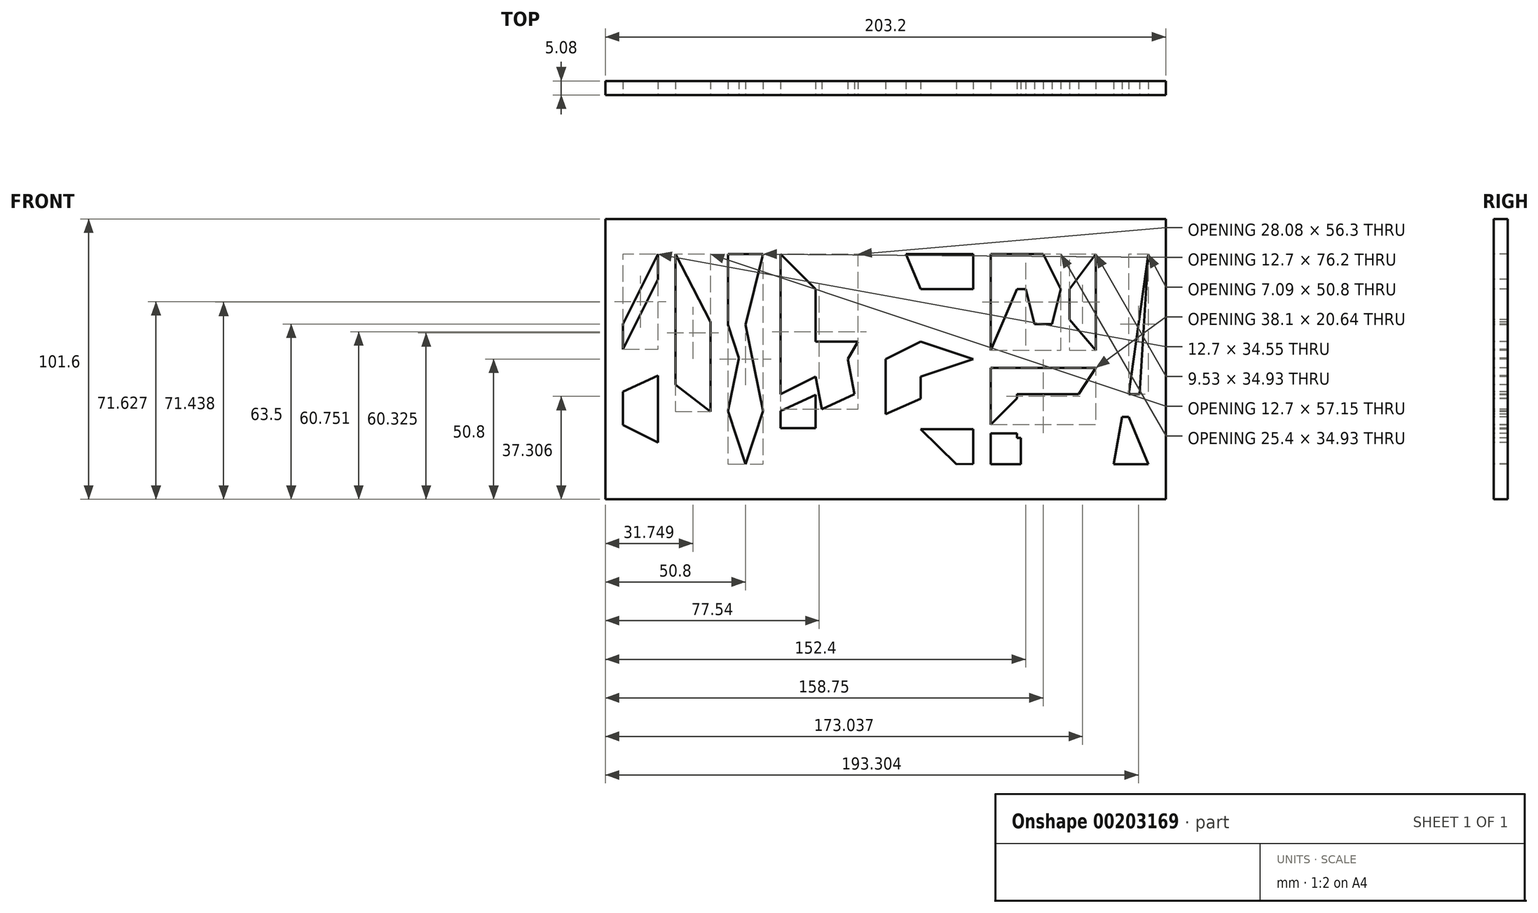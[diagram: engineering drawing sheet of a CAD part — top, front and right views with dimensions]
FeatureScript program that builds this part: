
annotation { "Feature Type Name" : "Feature", "Feature Type Description" : "" }
export const myFeature = defineFeature(function(context is Context, id is Id, definition is map)
    precondition{}
    {
        {
            var Q0;
            Q0=qCreatedBy(makeId("Front.planeOp"),FACE);
            var sketch = newSketch(context, id + "F0", { "sketchPlane" : qUnion([Q0])});
            skLineSegment(sketch, "E0.bottom", {"start": v(0, 0) * mm, "end": v(220.66, 0) * mm, "construction": true});
            skLineSegment(sketch, "E0.top", {"start": v(0, 138.11) * mm, "end": v(220.66, 138.11) * mm, "construction": true});
            skLineSegment(sketch, "E0.left", {"start": v(0, 0) * mm, "end": v(0, 138.11) * mm, "construction": true});
            skLineSegment(sketch, "E0.right", {"start": v(220.66, 0) * mm, "end": v(220.66, 138.11) * mm, "construction": true});
            skSolve(sketch);
        }
        {
            var Q0;
            Q0=qCreatedBy(makeId("Front.planeOp"),FACE);
            var sketch = newSketch(context, id + "F1", { "sketchPlane" : qUnion([Q0])});
            skLineSegment(sketch, "E1.bottom", {"start": v(0, 0) * mm, "end": v(203.2, 0) * mm});
            skLineSegment(sketch, "E1.top", {"start": v(0, 101.6) * mm, "end": v(203.2, 101.6) * mm});
            skLineSegment(sketch, "E1.left", {"start": v(0, 0) * mm, "end": v(0, 101.6) * mm});
            skLineSegment(sketch, "E1.right", {"start": v(203.2, 0) * mm, "end": v(203.2, 101.6) * mm});
            skSolve(sketch);
        }
        {
            var Q0;
            Q0=makeQuery(id+"F1.imprint","IMPRINT",FACE,{"disambiguationData":[TD([[makeQuery(id+"F1.imprint","IMPRINT",EDGE,{"derivedFrom":sQuery(id+"F1.wireOp",EDGE,"E1.bottom")}),1.0]])]});
            extrude(context, id + "F2", {"entities" : qUnion([Q0]), "oppositeDirection" : true, "depth" : 5.08 * mm});
        }
        {
            var Q0;
            Q0=makeQuery(id+"F2.opExtrude","CAP_FACE",FACE,{"disambiguationData":[OSD([sQuery(id+"F1.wireOp",EDGE,"E1.bottom"),sQuery(id+"F1.wireOp",EDGE,"E1.top"),sQuery(id+"F1.wireOp",EDGE,"E1.left"),sQuery(id+"F1.wireOp",EDGE,"E1.right")])],"isStart":true});
            var sketch = newSketch(context, id + "F3", { "sketchPlane" : qUnion([Q0])});
            skLineSegment(sketch, "E2", {"start": v(0, 50.8) * mm, "end": v(203.2, 50.8) * mm, "construction": true});
            skLineSegment(sketch, "E3", {"start": v(6.35, 88.9) * mm, "end": v(19.05, 88.9) * mm});
            skLineSegment(sketch, "E4", {"start": v(19.05, 88.9) * mm, "end": v(19.05, 50.8) * mm});
            skLineSegment(sketch, "E5", {"start": v(19.05, 50.8) * mm, "end": v(25.4, 50.8) * mm});
            skLineSegment(sketch, "E6", {"start": v(25.4, 50.8) * mm, "end": v(25.4, 88.9) * mm});
            skLineSegment(sketch, "E7", {"start": v(25.4, 88.9) * mm, "end": v(38.1, 88.9) * mm});
            skLineSegment(sketch, "E8", {"start": v(38.1, 88.9) * mm, "end": v(38.1, 50.8) * mm});
            skLineSegment(sketch, "E9", {"start": v(38.1, 50.8) * mm, "end": v(38.1, 12.7) * mm});
            skLineSegment(sketch, "E10", {"start": v(38.1, 12.7) * mm, "end": v(25.4, 12.7) * mm});
            skLineSegment(sketch, "E11", {"start": v(25.4, 12.7) * mm, "end": v(25.4, 31.75) * mm});
            skLineSegment(sketch, "E12", {"start": v(25.4, 31.75) * mm, "end": v(19.05, 31.75) * mm});
            skLineSegment(sketch, "E13", {"start": v(19.05, 31.75) * mm, "end": v(19.05, 12.7) * mm});
            skLineSegment(sketch, "E14", {"start": v(19.05, 12.7) * mm, "end": v(6.35, 12.7) * mm});
            skLineSegment(sketch, "E15", {"start": v(44.45, 88.9) * mm, "end": v(44.45, 12.7) * mm});
            skLineSegment(sketch, "E16", {"start": v(44.45, 12.7) * mm, "end": v(57.15, 12.7) * mm});
            skLineSegment(sketch, "E17", {"start": v(57.15, 12.7) * mm, "end": v(57.15, 88.9) * mm});
            skLineSegment(sketch, "E18", {"start": v(57.15, 88.9) * mm, "end": v(44.45, 88.9) * mm});
            skLineSegment(sketch, "E19", {"start": v(63.5, 88.9) * mm, "end": v(63.5, 12.7) * mm});
            skPoint(sketch, "E19.startSnap0", {"position": v(50.8, 88.9) * mm});
            skLineSegment(sketch, "E20", {"start": v(63.5, 12.7) * mm, "end": v(76.2, 12.7) * mm});
            skLineSegment(sketch, "E21", {"start": v(76.2, 12.7) * mm, "end": v(76.2, 44.45) * mm});
            skLineSegment(sketch, "E22", {"start": v(76.2, 44.45) * mm, "end": v(82.32, 12.7) * mm});
            skLineSegment(sketch, "E23", {"start": v(82.32, 12.7) * mm, "end": v(95.25, 12.7) * mm});
            skLineSegment(sketch, "E24", {"start": v(95.25, 12.7) * mm, "end": v(87.91, 50.8) * mm});
            skLineSegment(sketch, "E25", {"start": v(87.91, 50.8) * mm, "end": v(95.25, 63.5) * mm});
            skLineSegment(sketch, "E26", {"start": v(95.25, 63.5) * mm, "end": v(95.25, 88.9) * mm});
            skLineSegment(sketch, "E27", {"start": v(95.25, 88.9) * mm, "end": v(63.5, 88.9) * mm});
            skLineSegment(sketch, "E28", {"start": v(101.6, 88.9) * mm, "end": v(101.6, 12.7) * mm});
            skLineSegment(sketch, "E29", {"start": v(101.6, 12.7) * mm, "end": v(133.35, 12.7) * mm});
            skLineSegment(sketch, "E30", {"start": v(133.35, 12.7) * mm, "end": v(133.35, 25.4) * mm});
            skLineSegment(sketch, "E31", {"start": v(133.35, 25.4) * mm, "end": v(114.3, 25.4) * mm});
            skLineSegment(sketch, "E32", {"start": v(114.3, 25.4) * mm, "end": v(114.3, 44.45) * mm});
            skLineSegment(sketch, "E33", {"start": v(114.3, 44.45) * mm, "end": v(133.35, 44.45) * mm});
            skLineSegment(sketch, "E34", {"start": v(133.35, 44.45) * mm, "end": v(133.35, 57.15) * mm});
            skLineSegment(sketch, "E35", {"start": v(133.35, 57.15) * mm, "end": v(114.3, 57.15) * mm});
            skLineSegment(sketch, "E36", {"start": v(114.3, 57.15) * mm, "end": v(114.3, 76.2) * mm});
            skLineSegment(sketch, "E37", {"start": v(114.3, 76.2) * mm, "end": v(133.35, 76.2) * mm});
            skLineSegment(sketch, "E38", {"start": v(133.35, 76.2) * mm, "end": v(133.35, 88.9) * mm});
            skLineSegment(sketch, "E39", {"start": v(133.35, 88.9) * mm, "end": v(101.6, 88.9) * mm});
            skLineSegment(sketch, "E40", {"start": v(139.7, 88.9) * mm, "end": v(177.8, 88.9) * mm});
            skLineSegment(sketch, "E41", {"start": v(177.8, 88.9) * mm, "end": v(177.8, 53.98) * mm});
            skLineSegment(sketch, "E42", {"start": v(168.28, 53.98) * mm, "end": v(168.28, 76.2) * mm});
            skLineSegment(sketch, "E43", {"start": v(149.23, 76.2) * mm, "end": v(149.23, 53.98) * mm});
            skLineSegment(sketch, "E44", {"start": v(139.7, 12.7) * mm, "end": v(177.8, 12.7) * mm});
            skLineSegment(sketch, "E45", {"start": v(177.8, 12.7) * mm, "end": v(177.8, 22.23) * mm});
            skLineSegment(sketch, "E46", {"start": v(177.8, 22.23) * mm, "end": v(149.23, 22.23) * mm});
            skLineSegment(sketch, "E47", {"start": v(149.23, 22.23) * mm, "end": v(149.23, 23.81) * mm});
            skLineSegment(sketch, "E48", {"start": v(149.23, 36.51) * mm, "end": v(149.23, 38.1) * mm});
            skLineSegment(sketch, "E49", {"start": v(149.23, 38.1) * mm, "end": v(177.8, 38.1) * mm});
            skLineSegment(sketch, "E50", {"start": v(177.8, 38.1) * mm, "end": v(177.8, 47.63) * mm});
            skLineSegment(sketch, "E51", {"start": v(6.35, 88.9) * mm, "end": v(6.35, 12.7) * mm});
            skLineSegment(sketch, "E52", {"start": v(149.23, 76.2) * mm, "end": v(152.4, 76.2) * mm});
            skLineSegment(sketch, "E53", {"start": v(152.4, 76.2) * mm, "end": v(155.57, 63.5) * mm});
            skLineSegment(sketch, "E54", {"start": v(155.57, 63.5) * mm, "end": v(161.93, 63.5) * mm});
            skLineSegment(sketch, "E55", {"start": v(161.93, 63.5) * mm, "end": v(165.1, 76.2) * mm});
            skLineSegment(sketch, "E56", {"start": v(165.1, 76.2) * mm, "end": v(168.28, 76.2) * mm});
            skPoint(sketch, "E57", {"position": v(158.75, 88.9) * mm});
            skPoint(sketch, "E58", {"position": v(158.75, 63.5) * mm});
            skLineSegment(sketch, "E59", {"start": v(161.93, 33.34) * mm, "end": v(161.93, 26.99) * mm});
            skPoint(sketch, "E60", {"position": v(161.93, 30.16) * mm});
            skLineSegment(sketch, "E61", {"start": v(139.7, 88.9) * mm, "end": v(139.7, 53.98) * mm});
            skLineSegment(sketch, "E62", {"start": v(139.7, 53.98) * mm, "end": v(149.23, 53.98) * mm});
            skLineSegment(sketch, "E63", {"start": v(168.28, 53.98) * mm, "end": v(177.8, 53.98) * mm});
            skLineSegment(sketch, "E64", {"start": v(139.7, 47.63) * mm, "end": v(177.8, 47.63) * mm});
            skLineSegment(sketch, "E65", {"start": v(139.7, 47.63) * mm, "end": v(139.7, 12.7) * mm});
            skLineSegment(sketch, "E66", {"start": v(161.93, 33.34) * mm, "end": v(149.23, 36.51) * mm});
            skLineSegment(sketch, "E67", {"start": v(149.23, 23.81) * mm, "end": v(161.93, 26.99) * mm});
            skPoint(sketch, "E68", {"position": v(139.7, 30.16) * mm});
            skLineSegment(sketch, "E69", {"start": v(184.15, 88.9) * mm, "end": v(196.85, 88.9) * mm});
            skLineSegment(sketch, "E70", {"start": v(196.85, 88.9) * mm, "end": v(193.67, 38.1) * mm});
            skLineSegment(sketch, "E71", {"start": v(193.67, 38.1) * mm, "end": v(187.33, 38.1) * mm});
            skLineSegment(sketch, "E72", {"start": v(187.33, 38.1) * mm, "end": v(184.15, 88.9) * mm});
            skPoint(sketch, "E73", {"position": v(190.5, 88.9) * mm});
            skPoint(sketch, "E74", {"position": v(190.5, 38.1) * mm});
            skLineSegment(sketch, "E75", {"start": v(187.32, 29.85) * mm, "end": v(184.15, 12.7) * mm});
            skLineSegment(sketch, "E76", {"start": v(184.15, 12.7) * mm, "end": v(196.85, 12.7) * mm});
            skLineSegment(sketch, "E77", {"start": v(196.85, 12.7) * mm, "end": v(193.68, 29.85) * mm});
            skLineSegment(sketch, "E78", {"start": v(193.67, 29.85) * mm, "end": v(187.33, 29.85) * mm});
            skPoint(sketch, "E79", {"position": v(190.5, 29.85) * mm});
            skPoint(sketch, "E80", {"position": v(190.5, 12.7) * mm});
            skLineSegment(sketch, "E81", {"start": v(76.2, 57.15) * mm, "end": v(76.2, 76.2) * mm});
            skLineSegment(sketch, "E82", {"start": v(76.2, 76.2) * mm, "end": v(83.54, 76.2) * mm});
            skLineSegment(sketch, "E83", {"start": v(83.54, 76.2) * mm, "end": v(83.54, 69.85) * mm});
            skLineSegment(sketch, "E84", {"start": v(83.54, 69.85) * mm, "end": v(76.2, 57.15) * mm});
            skSolve(sketch);
        }
        {
            var Q0;
            Q0=makeQuery(id+"F3.imprint","IMPRINT",FACE,{"disambiguationData":[TD([[makeQuery(id+"F3.imprint","IMPRINT",EDGE,{"derivedFrom":sQuery(id+"F3.wireOp",EDGE,"E3")}),1.0]])]});
            var sketch = newSketch(context, id + "F4", { "sketchPlane" : qUnion([Q0])});
            skLineSegment(sketch, "E85", {"start": v(6.35, 63.49) * mm, "end": v(19.05, 88.9) * mm});
            skLineSegment(sketch, "E86", {"start": v(19.05, 88.9) * mm, "end": v(6.35, 88.9) * mm});
            skLineSegment(sketch, "E87", {"start": v(6.35, 88.9) * mm, "end": v(6.35, 63.49) * mm});
            skLineSegment(sketch, "E88", {"start": v(6.35, 54.35) * mm, "end": v(19.05, 79.76) * mm});
            skLineSegment(sketch, "E89", {"start": v(19.05, 79.76) * mm, "end": v(19.05, 50.8) * mm});
            skLineSegment(sketch, "E90", {"start": v(6.35, 38.97) * mm, "end": v(6.35, 54.35) * mm});
            skLineSegment(sketch, "E91", {"start": v(19.05, 31.75) * mm, "end": v(19.05, 44.79) * mm});
            skLineSegment(sketch, "E92", {"start": v(25.4, 41.55) * mm, "end": v(38.1, 31.75) * mm});
            skLineSegment(sketch, "E93", {"start": v(6.35, 26.94) * mm, "end": v(19.05, 20.6) * mm});
            skLineSegment(sketch, "E94", {"start": v(19.05, 20.6) * mm, "end": v(19.05, 12.7) * mm});
            skLineSegment(sketch, "E95", {"start": v(19.05, 12.7) * mm, "end": v(6.35, 12.7) * mm});
            skLineSegment(sketch, "E96", {"start": v(6.35, 12.7) * mm, "end": v(6.35, 26.94) * mm});
            skLineSegment(sketch, "E97", {"start": v(19.05, 50.8) * mm, "end": v(25.4, 50.8) * mm});
            skLineSegment(sketch, "E98", {"start": v(25.4, 50.8) * mm, "end": v(25.4, 41.55) * mm});
            skLineSegment(sketch, "E99", {"start": v(6.35, 38.97) * mm, "end": v(19.05, 44.79) * mm});
            skLineSegment(sketch, "E100", {"start": v(38.1, 31.75) * mm, "end": v(38.1, 12.7) * mm});
            skLineSegment(sketch, "E101", {"start": v(38.1, 12.7) * mm, "end": v(25.4, 12.7) * mm});
            skLineSegment(sketch, "E102", {"start": v(25.4, 12.7) * mm, "end": v(25.4, 31.75) * mm});
            skLineSegment(sketch, "E103", {"start": v(25.4, 31.75) * mm, "end": v(19.05, 31.75) * mm});
            skLineSegment(sketch, "E104", {"start": v(25.4, 64.16) * mm, "end": v(25.4, 88.9) * mm});
            skLineSegment(sketch, "E105", {"start": v(25.4, 88.9) * mm, "end": v(38.12, 64.16) * mm});
            skLineSegment(sketch, "E106", {"start": v(38.12, 64.16) * mm, "end": v(25.4, 64.16) * mm});
            skLineSegment(sketch, "E107", {"start": v(44.45, 88.9) * mm, "end": v(44.45, 63.26) * mm});
            skLineSegment(sketch, "E108", {"start": v(44.45, 63.26) * mm, "end": v(48.35, 51.2) * mm});
            skLineSegment(sketch, "E109", {"start": v(48.35, 51.2) * mm, "end": v(44.45, 31.96) * mm});
            skLineSegment(sketch, "E110", {"start": v(44.45, 31.96) * mm, "end": v(50.8, 12.7) * mm});
            skLineSegment(sketch, "E111", {"start": v(50.8, 12.7) * mm, "end": v(57.15, 31.96) * mm});
            skLineSegment(sketch, "E112", {"start": v(57.15, 31.96) * mm, "end": v(53.25, 51.2) * mm});
            skLineSegment(sketch, "E113", {"start": v(53.25, 51.2) * mm, "end": v(50.8, 63.26) * mm});
            skLineSegment(sketch, "E114", {"start": v(50.8, 63.26) * mm, "end": v(57.15, 88.9) * mm});
            skLineSegment(sketch, "E115", {"start": v(57.15, 88.9) * mm, "end": v(44.45, 88.9) * mm});
            skLineSegment(sketch, "E116", {"start": v(63.5, 88.9) * mm, "end": v(76.2, 76.2) * mm});
            skLineSegment(sketch, "E117", {"start": v(76.2, 76.2) * mm, "end": v(76.2, 57.15) * mm});
            skLineSegment(sketch, "E118", {"start": v(63.5, 38.08) * mm, "end": v(63.5, 88.9) * mm});
            skLineSegment(sketch, "E119", {"start": v(63.5, 25.77) * mm, "end": v(63.5, 31.96) * mm});
            skLineSegment(sketch, "E120", {"start": v(63.5, 31.96) * mm, "end": v(76.2, 37.86) * mm});
            skLineSegment(sketch, "E121", {"start": v(76.2, 37.86) * mm, "end": v(76.2, 25.77) * mm});
            skLineSegment(sketch, "E122", {"start": v(76.2, 25.77) * mm, "end": v(63.5, 25.77) * mm});
            skLineSegment(sketch, "E123", {"start": v(76.2, 57.15) * mm, "end": v(91.58, 57.15) * mm});
            skLineSegment(sketch, "E124", {"start": v(91.58, 57.15) * mm, "end": v(87.91, 50.8) * mm});
            skLineSegment(sketch, "E125", {"start": v(76.2, 44.45) * mm, "end": v(63.5, 38.08) * mm});
            skLineSegment(sketch, "E126", {"start": v(78.48, 32.6) * mm, "end": v(90.35, 38.12) * mm});
            skLineSegment(sketch, "E127", {"start": v(114.3, 57.15) * mm, "end": v(101.6, 50.8) * mm});
            skLineSegment(sketch, "E128", {"start": v(101.6, 50.8) * mm, "end": v(114.3, 44.45) * mm});
            skLineSegment(sketch, "E129", {"start": v(114.3, 44.45) * mm, "end": v(133.35, 50.8) * mm});
            skLineSegment(sketch, "E130", {"start": v(133.35, 50.8) * mm, "end": v(114.3, 57.15) * mm});
            skLineSegment(sketch, "E131", {"start": v(114.3, 36.42) * mm, "end": v(101.6, 30.85) * mm});
            skLineSegment(sketch, "E132", {"start": v(101.6, 30.85) * mm, "end": v(101.6, 12.7) * mm});
            skLineSegment(sketch, "E133", {"start": v(101.6, 12.7) * mm, "end": v(127.23, 12.7) * mm});
            skLineSegment(sketch, "E134", {"start": v(127.23, 12.7) * mm, "end": v(114.3, 25.4) * mm});
            skLineSegment(sketch, "E135", {"start": v(114.3, 25.4) * mm, "end": v(114.3, 36.42) * mm});
            skLineSegment(sketch, "E136", {"start": v(108.95, 88.9) * mm, "end": v(114.3, 76.2) * mm});
            skLineSegment(sketch, "E137", {"start": v(114.3, 76.2) * mm, "end": v(133.35, 76.2) * mm});
            skLineSegment(sketch, "E138", {"start": v(133.35, 76.2) * mm, "end": v(133.35, 88.9) * mm});
            skLineSegment(sketch, "E139", {"start": v(133.35, 88.9) * mm, "end": v(108.95, 88.9) * mm});
            skLineSegment(sketch, "E140", {"start": v(152.4, 76.2) * mm, "end": v(158.75, 88.9) * mm});
            skLineSegment(sketch, "E141", {"start": v(158.75, 88.9) * mm, "end": v(165.1, 76.2) * mm});
            skLineSegment(sketch, "E142", {"start": v(165.1, 76.2) * mm, "end": v(161.93, 63.5) * mm});
            skLineSegment(sketch, "E143", {"start": v(161.93, 63.5) * mm, "end": v(155.57, 63.5) * mm});
            skLineSegment(sketch, "E144", {"start": v(155.57, 63.5) * mm, "end": v(152.4, 76.2) * mm});
            skLineSegment(sketch, "E145", {"start": v(168.28, 76.2) * mm, "end": v(177.8, 88.9) * mm});
            skLineSegment(sketch, "E146", {"start": v(177.8, 88.9) * mm, "end": v(177.8, 53.98) * mm});
            skLineSegment(sketch, "E147", {"start": v(177.8, 53.97) * mm, "end": v(168.27, 65.09) * mm});
            skLineSegment(sketch, "E148", {"start": v(168.28, 65.09) * mm, "end": v(168.28, 76.2) * mm});
            skLineSegment(sketch, "E149", {"start": v(139.7, 53.98) * mm, "end": v(149.23, 53.98) * mm});
            skLineSegment(sketch, "E150", {"start": v(149.23, 53.98) * mm, "end": v(149.23, 76.2) * mm});
            skLineSegment(sketch, "E151", {"start": v(149.23, 76.2) * mm, "end": v(139.7, 53.98) * mm});
            skLineSegment(sketch, "E152", {"start": v(139.7, 47.63) * mm, "end": v(177.8, 47.63) * mm});
            skLineSegment(sketch, "E153", {"start": v(177.8, 47.63) * mm, "end": v(171.66, 38.1) * mm});
            skLineSegment(sketch, "E154", {"start": v(171.66, 38.1) * mm, "end": v(149.23, 38.1) * mm});
            skLineSegment(sketch, "E155", {"start": v(139.7, 47.63) * mm, "end": v(139.7, 26.99) * mm});
            skLineSegment(sketch, "E156", {"start": v(139.7, 26.99) * mm, "end": v(149.23, 36.51) * mm});
            skLineSegment(sketch, "E157", {"start": v(149.23, 36.51) * mm, "end": v(149.23, 38.1) * mm});
            skLineSegment(sketch, "E158", {"start": v(150.7, 22.23) * mm, "end": v(150.7, 12.7) * mm});
            skLineSegment(sketch, "E159", {"start": v(150.7, 12.7) * mm, "end": v(139.7, 12.7) * mm});
            skLineSegment(sketch, "E160", {"start": v(139.7, 12.7) * mm, "end": v(139.7, 23.81) * mm});
            skLineSegment(sketch, "E161", {"start": v(139.7, 23.81) * mm, "end": v(149.23, 23.81) * mm});
            skLineSegment(sketch, "E162", {"start": v(149.23, 23.81) * mm, "end": v(149.23, 22.23) * mm});
            skLineSegment(sketch, "E163", {"start": v(149.23, 22.23) * mm, "end": v(150.7, 22.23) * mm});
            skLineSegment(sketch, "E164", {"start": v(187.33, 38.1) * mm, "end": v(187.33, 88.9) * mm});
            skLineSegment(sketch, "E165", {"start": v(187.33, 88.9) * mm, "end": v(184.15, 88.9) * mm});
            skLineSegment(sketch, "E166", {"start": v(184.15, 88.9) * mm, "end": v(187.33, 38.1) * mm});
            skLineSegment(sketch, "E167", {"start": v(189.76, 29.85) * mm, "end": v(196.85, 12.7) * mm});
            skLineSegment(sketch, "E168", {"start": v(196.85, 12.7) * mm, "end": v(193.68, 29.85) * mm});
            skLineSegment(sketch, "E169", {"start": v(193.68, 29.85) * mm, "end": v(189.76, 29.85) * mm});
            skLineSegment(sketch, "E170", {"start": v(189.76, 38.1) * mm, "end": v(196.85, 88.9) * mm});
            skLineSegment(sketch, "E171", {"start": v(196.85, 88.9) * mm, "end": v(193.68, 38.1) * mm});
            skLineSegment(sketch, "E172", {"start": v(193.67, 38.1) * mm, "end": v(189.76, 38.1) * mm});
            skLineSegment(sketch, "E173", {"start": v(48.35, 51.2) * mm, "end": v(53.25, 51.2) * mm, "construction": true});
            skPoint(sketch, "E174", {"position": v(50.8, 51.2) * mm});
            skLineSegment(sketch, "E175", {"start": v(57.15, 88.9) * mm, "end": v(57.15, 31.96) * mm});
            skLineSegment(sketch, "E176", {"start": v(50.8, 12.7) * mm, "end": v(57.15, 12.7) * mm});
            skLineSegment(sketch, "E177", {"start": v(57.15, 12.7) * mm, "end": v(57.15, 31.96) * mm});
            skLineSegment(sketch, "E178", {"start": v(50.8, 12.7) * mm, "end": v(44.45, 12.7) * mm});
            skLineSegment(sketch, "E179", {"start": v(44.45, 12.7) * mm, "end": v(44.45, 31.96) * mm});
            skLineSegment(sketch, "E180", {"start": v(44.45, 63.26) * mm, "end": v(44.45, 31.96) * mm});
            skLineSegment(sketch, "E181", {"start": v(63.5, 88.9) * mm, "end": v(95.29, 88.9) * mm});
            skLineSegment(sketch, "E182", {"start": v(95.29, 88.9) * mm, "end": v(95.29, 63.17) * mm});
            skLineSegment(sketch, "E183", {"start": v(95.29, 63.17) * mm, "end": v(91.58, 57.15) * mm});
            skLineSegment(sketch, "E184", {"start": v(76.2, 57.15) * mm, "end": v(83.54, 69.85) * mm});
            skLineSegment(sketch, "E185", {"start": v(83.54, 69.85) * mm, "end": v(83.54, 76.2) * mm});
            skLineSegment(sketch, "E186", {"start": v(83.54, 76.2) * mm, "end": v(76.2, 76.2) * mm});
            skLineSegment(sketch, "E187", {"start": v(63.5, 38.08) * mm, "end": v(63.5, 31.96) * mm});
            skLineSegment(sketch, "E188", {"start": v(63.5, 25.77) * mm, "end": v(63.5, 12.87) * mm});
            skLineSegment(sketch, "E189", {"start": v(63.5, 12.87) * mm, "end": v(76.2, 12.87) * mm});
            skLineSegment(sketch, "E190", {"start": v(76.2, 12.87) * mm, "end": v(76.2, 25.77) * mm});
            skLineSegment(sketch, "E191", {"start": v(78.48, 32.6) * mm, "end": v(82.53, 12.66) * mm});
            skLineSegment(sketch, "E192", {"start": v(82.53, 12.66) * mm, "end": v(95.17, 12.66) * mm});
            skLineSegment(sketch, "E193", {"start": v(95.17, 12.66) * mm, "end": v(90.35, 38.12) * mm});
            skLineSegment(sketch, "E194", {"start": v(76.2, 44.45) * mm, "end": v(78.48, 32.6) * mm});
            skLineSegment(sketch, "E195", {"start": v(90.35, 38.12) * mm, "end": v(87.91, 50.8) * mm});
            skLineSegment(sketch, "E196", {"start": v(76.2, 37.86) * mm, "end": v(76.2, 44.45) * mm});
            skLineSegment(sketch, "E197", {"start": v(108.95, 88.9) * mm, "end": v(101.6, 88.9) * mm});
            skLineSegment(sketch, "E198", {"start": v(101.6, 88.9) * mm, "end": v(101.6, 50.8) * mm});
            skLineSegment(sketch, "E199", {"start": v(101.6, 50.8) * mm, "end": v(101.6, 30.85) * mm});
            skLineSegment(sketch, "E200", {"start": v(114.3, 36.42) * mm, "end": v(114.3, 44.45) * mm});
            skLineSegment(sketch, "E201", {"start": v(114.3, 44.45) * mm, "end": v(133.35, 44.45) * mm});
            skLineSegment(sketch, "E202", {"start": v(133.35, 44.45) * mm, "end": v(133.35, 50.8) * mm});
            skLineSegment(sketch, "E203", {"start": v(133.35, 50.8) * mm, "end": v(133.35, 57.15) * mm});
            skLineSegment(sketch, "E204", {"start": v(133.35, 57.15) * mm, "end": v(114.3, 57.15) * mm});
            skLineSegment(sketch, "E205", {"start": v(114.3, 57.15) * mm, "end": v(114.3, 76.2) * mm});
            skLineSegment(sketch, "E206", {"start": v(114.3, 25.4) * mm, "end": v(133.35, 25.4) * mm});
            skLineSegment(sketch, "E207", {"start": v(133.35, 25.4) * mm, "end": v(133.35, 12.76) * mm});
            skLineSegment(sketch, "E208", {"start": v(133.35, 12.76) * mm, "end": v(127.23, 12.7) * mm});
            skLineSegment(sketch, "E209", {"start": v(150.7, 12.7) * mm, "end": v(177.8, 12.7) * mm});
            skLineSegment(sketch, "E210", {"start": v(177.8, 12.7) * mm, "end": v(177.8, 22.23) * mm});
            skLineSegment(sketch, "E211", {"start": v(177.8, 22.23) * mm, "end": v(150.7, 22.23) * mm});
            skLineSegment(sketch, "E212", {"start": v(149.23, 23.81) * mm, "end": v(161.93, 26.99) * mm});
            skLineSegment(sketch, "E213", {"start": v(161.93, 33.34) * mm, "end": v(149.23, 36.51) * mm});
            skLineSegment(sketch, "E214", {"start": v(139.7, 23.81) * mm, "end": v(139.7, 26.99) * mm});
            skLineSegment(sketch, "E215", {"start": v(171.66, 38.1) * mm, "end": v(177.8, 38.1) * mm});
            skLineSegment(sketch, "E216", {"start": v(177.8, 38.1) * mm, "end": v(177.8, 47.63) * mm});
            skLineSegment(sketch, "E217", {"start": v(139.7, 53.98) * mm, "end": v(139.7, 88.9) * mm});
            skLineSegment(sketch, "E218", {"start": v(139.7, 88.9) * mm, "end": v(158.75, 88.9) * mm});
            skLineSegment(sketch, "E219", {"start": v(149.22, 76.2) * mm, "end": v(149.22, 76.2) * mm});
            skLineSegment(sketch, "E220", {"start": v(149.23, 76.2) * mm, "end": v(152.4, 76.2) * mm});
            skLineSegment(sketch, "E221", {"start": v(158.75, 88.9) * mm, "end": v(177.8, 88.9) * mm});
            skLineSegment(sketch, "E222", {"start": v(168.28, 76.2) * mm, "end": v(165.1, 76.2) * mm});
            skLineSegment(sketch, "E223", {"start": v(168.28, 65.09) * mm, "end": v(168.28, 53.98) * mm});
            skLineSegment(sketch, "E224", {"start": v(168.28, 53.98) * mm, "end": v(177.8, 53.98) * mm});
            skLineSegment(sketch, "E225", {"start": v(187.33, 88.9) * mm, "end": v(196.85, 88.9) * mm});
            skLineSegment(sketch, "E226", {"start": v(189.76, 38.1) * mm, "end": v(187.33, 38.1) * mm});
            skLineSegment(sketch, "E227", {"start": v(189.76, 29.85) * mm, "end": v(187.33, 29.85) * mm});
            skLineSegment(sketch, "E228", {"start": v(187.33, 29.85) * mm, "end": v(184.3, 12.7) * mm});
            skLineSegment(sketch, "E229", {"start": v(184.3, 12.7) * mm, "end": v(196.85, 12.7) * mm});
            skLineSegment(sketch, "E230", {"start": v(161.93, 26.99) * mm, "end": v(161.93, 33.34) * mm});
            skLineSegment(sketch, "E231", {"start": v(19.05, 20.6) * mm, "end": v(19.05, 31.75) * mm});
            skLineSegment(sketch, "E232", {"start": v(6.35, 38.97) * mm, "end": v(6.35, 26.94) * mm});
            skLineSegment(sketch, "E233", {"start": v(6.35, 54.35) * mm, "end": v(6.35, 63.49) * mm});
            skLineSegment(sketch, "E234", {"start": v(25.4, 88.9) * mm, "end": v(38.1, 88.9) * mm});
            skLineSegment(sketch, "E235", {"start": v(38.1, 88.9) * mm, "end": v(38.12, 64.16) * mm});
            skLineSegment(sketch, "E236", {"start": v(38.1, 31.75) * mm, "end": v(38.12, 64.16) * mm});
            skLineSegment(sketch, "E237", {"start": v(25.4, 50.8) * mm, "end": v(25.4, 64.16) * mm});
            skLineSegment(sketch, "E238", {"start": v(44.45, 31.96) * mm, "end": v(44.45, 12.7) * mm});
            skLineSegment(sketch, "E239", {"start": v(57.15, 31.96) * mm, "end": v(57.15, 12.7) * mm});
            skSolve(sketch);
        }
        {
            var Q0;
            {var subQ0=sQuery(id+"F4.wireOp",EDGE,"E85");Q0=makeQuery(id+"F4.imprint","IMPRINT",FACE,{"disambiguationData":[TD([[makeQuery(id+"F4.imprint","IMPRINT",EDGE,{"derivedFrom":subQ0}),-1.0]])]});}
            var Q1;
            {var subQ0=sQuery(id+"F4.wireOp",EDGE,"E104");Q1=makeQuery(id+"F4.imprint","IMPRINT",FACE,{"disambiguationData":[TD([[makeQuery(id+"F4.imprint","IMPRINT",EDGE,{"derivedFrom":subQ0}),-1.0]])]});}
            var Q2;
            Q2=makeQuery(id+"F4.imprint","IMPRINT",FACE,{"disambiguationData":[TD([[makeQuery(id+"F4.imprint","IMPRINT",EDGE,{"derivedFrom":sQuery(id+"F4.wireOp",EDGE,"E91")}),1.0]])]});
            var Q3;
            {var subQ6=sQuery(id+"F4.wireOp",EDGE,"E92");Q3=makeQuery(id+"F4.imprint","IMPRINT",FACE,{"disambiguationData":[TD([[makeQuery(id+"F4.imprint","IMPRINT",EDGE,{"derivedFrom":subQ6}),1.0]])]});}
            var Q4;
            Q4=makeQuery(id+"F4.imprint","IMPRINT",FACE,{"disambiguationData":[TD([[makeQuery(id+"F4.imprint","IMPRINT",EDGE,{"derivedFrom":sQuery(id+"F4.wireOp",EDGE,"E107")}),1.0]])]});
            var Q5;
            Q5=makeQuery(id+"F4.imprint","IMPRINT",FACE,{"disambiguationData":[TD([[makeQuery(id+"F4.imprint","IMPRINT",EDGE,{"derivedFrom":sQuery(id+"F4.wireOp",EDGE,"E116")}),-1.0]])]});
            var Q6;
            Q6=makeQuery(id+"F4.imprint","IMPRINT",FACE,{"disambiguationData":[TD([[makeQuery(id+"F4.imprint","IMPRINT",EDGE,{"derivedFrom":sQuery(id+"F4.wireOp",EDGE,"E119")}),1.0]])]});
            var Q7;
            Q7=makeQuery(id+"F4.imprint","IMPRINT",FACE,{"disambiguationData":[TD([[makeQuery(id+"F4.imprint","IMPRINT",EDGE,{"derivedFrom":sQuery(id+"F4.wireOp",EDGE,"E127")}),1.0]])]});
            var Q8;
            Q8=makeQuery(id+"F4.imprint","IMPRINT",FACE,{"disambiguationData":[TD([[makeQuery(id+"F4.imprint","IMPRINT",EDGE,{"derivedFrom":sQuery(id+"F4.wireOp",EDGE,"E134")}),-1.0]])]});
            var Q9;
            Q9=makeQuery(id+"F4.imprint","IMPRINT",FACE,{"disambiguationData":[TD([[makeQuery(id+"F4.imprint","IMPRINT",EDGE,{"derivedFrom":sQuery(id+"F4.wireOp",EDGE,"E128")}),-1.0]])]});
            var Q10;
            Q10=makeQuery(id+"F4.imprint","IMPRINT",FACE,{"disambiguationData":[TD([[makeQuery(id+"F4.imprint","IMPRINT",EDGE,{"derivedFrom":sQuery(id+"F4.wireOp",EDGE,"E140")}),-1.0]])]});
            var Q11;
            Q11=makeQuery(id+"F4.imprint","IMPRINT",FACE,{"disambiguationData":[TD([[makeQuery(id+"F4.imprint","IMPRINT",EDGE,{"derivedFrom":sQuery(id+"F4.wireOp",EDGE,"E140")}),1.0]])]});
            var Q12;
            Q12=makeQuery(id+"F4.imprint","IMPRINT",FACE,{"disambiguationData":[TD([[makeQuery(id+"F4.imprint","IMPRINT",EDGE,{"derivedFrom":sQuery(id+"F4.wireOp",EDGE,"E145")}),-1.0]])]});
            var Q13;
            Q13=makeQuery(id+"F4.imprint","IMPRINT",FACE,{"disambiguationData":[TD([[makeQuery(id+"F4.imprint","IMPRINT",EDGE,{"derivedFrom":sQuery(id+"F4.wireOp",EDGE,"E152")}),-1.0]])]});
            var Q14;
            Q14=makeQuery(id+"F4.imprint","IMPRINT",FACE,{"disambiguationData":[TD([[makeQuery(id+"F4.imprint","IMPRINT",EDGE,{"derivedFrom":sQuery(id+"F4.wireOp",EDGE,"E158")}),-1.0]])]});
            var Q15;
            Q15=makeQuery(id+"F4.imprint","IMPRINT",FACE,{"disambiguationData":[TD([[makeQuery(id+"F4.imprint","IMPRINT",EDGE,{"derivedFrom":sQuery(id+"F4.wireOp",EDGE,"E167")}),-1.0]])]});
            var Q16;
            Q16=makeQuery(id+"F4.imprint","IMPRINT",FACE,{"disambiguationData":[TD([[makeQuery(id+"F4.imprint","IMPRINT",EDGE,{"derivedFrom":sQuery(id+"F4.wireOp",EDGE,"E170")}),-1.0]])]});
            var Q17;
            Q17=makeQuery(id+"F4.imprint","IMPRINT",FACE,{"disambiguationData":[TD([[makeQuery(id+"F4.imprint","IMPRINT",EDGE,{"derivedFrom":sQuery(id+"F4.wireOp",EDGE,"E136")}),1.0]])]});
            extrude(context, id + "F5", {"entities" : qUnion([Q0, Q1, Q2, Q3, Q4, Q5, Q6, Q7, Q8, Q9, Q10, Q11, Q12, Q13, Q14, Q15, Q16, Q17]), "operationType" : NewBodyOperationType.REMOVE, "oppositeDirection" : true, "depth" : 25.4 * mm});
        }
    });
